# Revit family: NBS_Allermuir_DmstcChrs_Mozaik-en-us
name_source: partatom
category: Furniture
revit_build: Autodesk Revit 2016 (Build: 20151007_0715(x64)
units: mm (PartAtom-declared; Revit-internal decimal feet)

## family parameters
Always vertical = Yes
Cut with Voids When Loaded = No
Room Calculation Point = No
Shared = No
Work Plane-Based = No

## types (5) — shared parameters
AssetType = Moveable
Category = Pr_40_50_12_22:Dining chairs
CodePerformance = ANSI/BIFMA X5.4:2012
DurationUnit = year
EnvironmentalProductDeclaration = http://www.thesenatorgroup.com
ExpectedLife = 10
Features = Traditional carcass construction, fully upholstred, wire frame finished in black powder coat, plastic glides, wire frame available in white, coral or pebble powder coat, two tone upholstery
FrameColourOptions = White, coral, pebble
FrameFinishOptions = Two tone upholstery
FramesColour = Black
FramesFinish = Powder coat
FramesMaterial = Steel
IfcExportAs = IfcFurnitureType
IfcExportType = SOFA
IntegralAccessories = Plastic glides
IsBuiltIn = No
LegMaterial = NBS_Concept
ManufacturerName = Allermuir
ManufacturerURL = http://www.thesenatorgroup.com
ModelReference = Mozaik
NBSCertification = www.nationalbimlibrary.com/cert/ioimizft
NBSDescription = Domestic chairs
NBSReference = 45-35-20/365
OmniClassCode = 22-12 52 23
OmniClassTitle = Office Seating
OmniClassVersion = Table 22 2012-05-16
ProductInformation = http://www.thesenatorgroup.com
SeatMaterial = NBS_Concept
SeatsAndBacksFinish = Fully upholstered
Status = UNSET
Uniclass2015Code = Pr_40_50_12_22
Uniclass2015Title = Dining chairs
Uniclass2015Version = Products v1.9
Version = 1
WarrantyDescription = Allermuir warrant that its manufactured products are free from manufacturing defects in materials or workmanship for a period of ten years
WarrantyDurationParts = 10
WarrantyDurationUnit = year
zero-valued in all types: HighestSeatingHeight, LowestSeatingHeight

## per-type parameters (varying)
| type | BIMObjectName | Description | Name | NominalDepth | NominalHeight | NominalLength | NominalWidth | SeatingHeight | Size |
| MZK101 | NBS_Allermuir_DomesticChairs_Mozaik_MZK101-US | Low square stool, small | DomesticChairs_Mozaik_MZK101-US_Allermuir | 17 " | 17 " | 17 " | 17 " | 17 " | 17.25 x 17.25 x 16.5" |
| MZK201 | NBS_Allermuir_DomesticChairs_Mozaik_MZK201-US | High square stool, small | DomesticChairs_Mozaik_MZK201-US_Allermuir | 17 " | 24 " | 17 " | 17 " | 24 " | 17.25 x 17.25 x 23.5" |
| MZK102 | NBS_Allermuir_DomesticChairs_Mozaik_MZK102-US | Low square stool, large | DomesticChairs_Mozaik_MZK102-US_Allermuir | 34 " | 17 " | 34 " | 34 " | 17 " | 34 x 34 x 16.5" |
| MZK103 | NBS_Allermuir_DomesticChairs_Mozaik_MZK103-US | Low rectangular bench | DomesticChairs_Mozaik_MZK103-US_Allermuir | 17 " | 17 " | 34 " | 17 " | 17 " | 34 x 17.25 x 16.5" |
| MZK203 | NBS_Allermuir_DomesticChairs_Mozaik_MZK203-US | High rectangular bench | DomesticChairs_Mozaik_MZK203-US_Allermuir | 17 " | 24 " | 34 " | 17 " | 24 " | 34 x 17.25 x 23.5" |

note: column(s) folded — value = type name in every type: ModelNumber

## geometry (parser evidence)
native form markers: Sweep x3
no freeform markers — native parametric forms only
